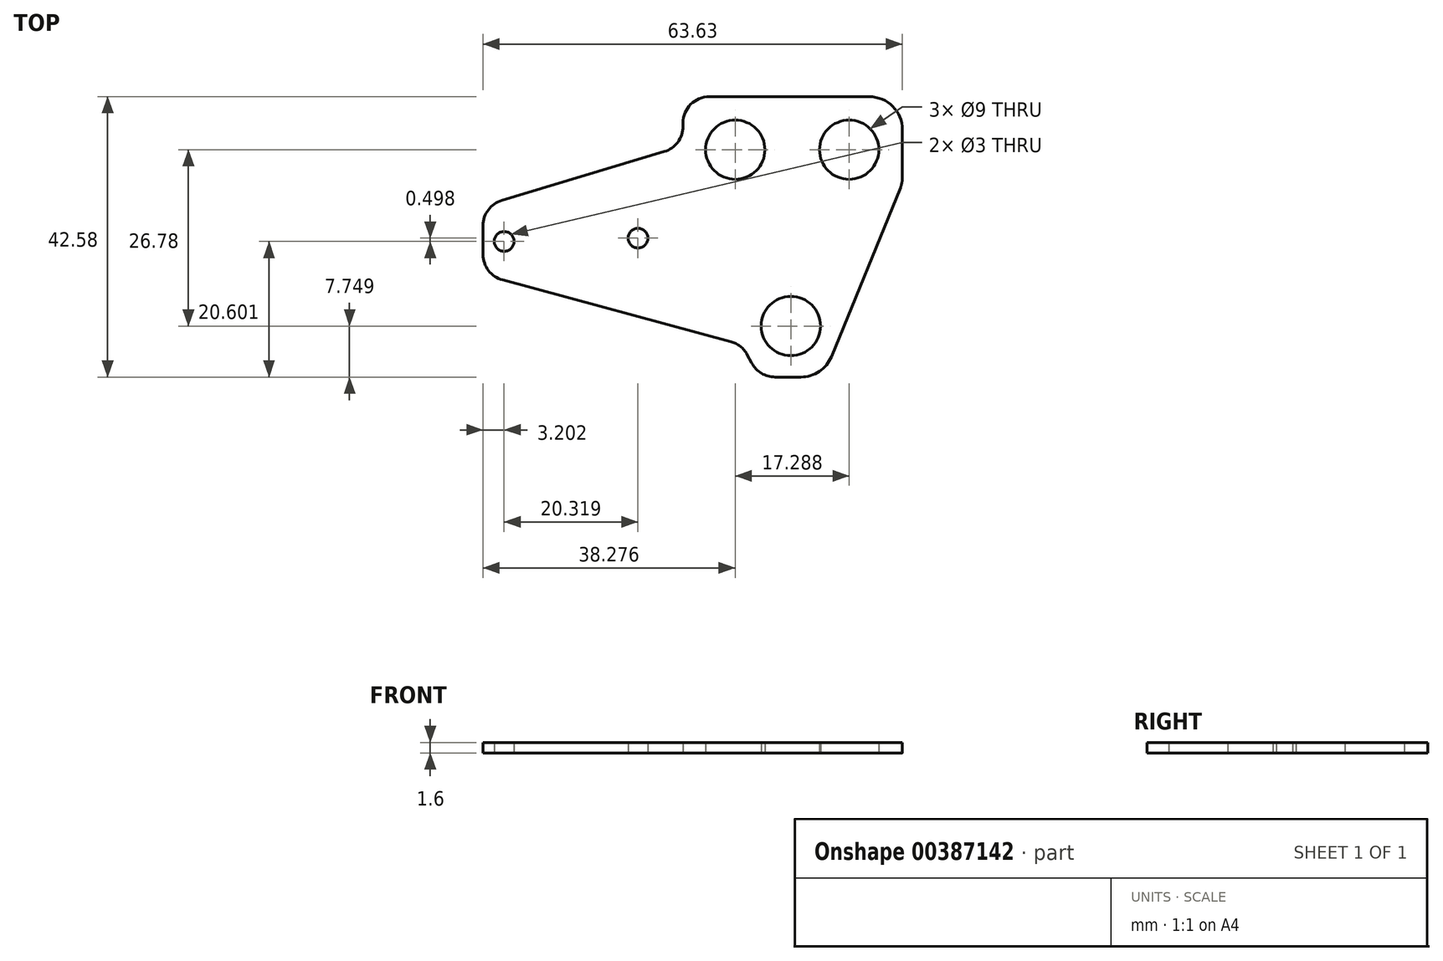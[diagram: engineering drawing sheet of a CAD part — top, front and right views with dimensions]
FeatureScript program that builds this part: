
annotation { "Feature Type Name" : "Feature", "Feature Type Description" : "" }
export const myFeature = defineFeature(function(context is Context, id is Id, definition is map)
    precondition{}
    {
        {
            var Q0;
            Q0=qCreatedBy(makeId("Top.planeOp"),FACE);
            var sketch = newSketch(context, id + "F0", { "sketchPlane" : qUnion([Q0])});
            skLineSegment(sketch, "E0", {"start": v(31.23, -1.42) * mm, "end": v(31.23, -8.72) * mm});
            skLineSegment(sketch, "E1", {"start": v(30.94, -10.23) * mm, "end": v(20.46, -35.89) * mm});
            skLineSegment(sketch, "E2", {"start": v(15.83, -39) * mm, "end": v(11.9, -39) * mm});
            skLineSegment(sketch, "E3", {"start": v(8.39, -36.9) * mm, "end": v(7.68, -35.58) * mm});
            skLineSegment(sketch, "E4", {"start": v(5.2, -33.62) * mm, "end": v(-29.44, -24.24) * mm});
            skLineSegment(sketch, "E5", {"start": v(-32.4, -20.38) * mm, "end": v(-32.4, -15.99) * mm});
            skLineSegment(sketch, "E6", {"start": v(-29.55, -12.16) * mm, "end": v(-4.9, -4.77) * mm});
            skLineSegment(sketch, "E7", {"start": v(-2.05, -0.93) * mm, "end": v(-2.05, -0.42) * mm});
            skLineSegment(sketch, "E8", {"start": v(1.95, 3.58) * mm, "end": v(26.23, 3.58) * mm});
            skCircle(sketch, "E9", {"center": v(23.16, -4.47) * mm, "radius": 4.5 * mm});
            skCircle(sketch, "E10", {"center": v(5.88, -4.47) * mm, "radius": 4.5 * mm});
            skCircle(sketch, "E11", {"center": v(14.32, -31.25) * mm, "radius": 4.5 * mm});
            skCircle(sketch, "E12", {"center": v(-29.2, -18.4) * mm, "radius": 1.5 * mm});
            skCircle(sketch, "E13", {"center": v(-8.88, -17.9) * mm, "radius": 1.5 * mm});
            skArc(sketch, "E14.filletArc", {"start": v(31.23, -1.42) * mm, "mid": v(29.77, 2.12) * mm, "end": v(26.23, 3.58) * mm});
            skArc(sketch, "E15.filletArc", {"start": v(15.83, -39) * mm, "mid": v(18.62, -38.15) * mm, "end": v(20.46, -35.89) * mm});
            skArc(sketch, "E16.filletArc", {"start": v(-29.55, -12.16) * mm, "mid": v(-31.6, -13.6) * mm, "end": v(-32.4, -15.99) * mm});
            skArc(sketch, "E17.filletArc", {"start": v(-32.4, -20.38) * mm, "mid": v(-31.57, -22.81) * mm, "end": v(-29.44, -24.24) * mm});
            skArc(sketch, "E18.filletArc", {"start": v(-4.9, -4.77) * mm, "mid": v(-2.84, -3.32) * mm, "end": v(-2.05, -0.93) * mm});
            skArc(sketch, "E19.filletArc", {"start": v(1.95, 3.58) * mm, "mid": v(-0.88, 2.41) * mm, "end": v(-2.05, -0.42) * mm});
            skArc(sketch, "E20.filletArc", {"start": v(8.39, -36.9) * mm, "mid": v(9.86, -38.43) * mm, "end": v(11.9, -39) * mm});
            skArc(sketch, "E21.filletArc", {"start": v(7.68, -35.58) * mm, "mid": v(6.64, -34.34) * mm, "end": v(5.2, -33.62) * mm});
            skArc(sketch, "E22.filletArc", {"start": v(30.94, -10.23) * mm, "mid": v(31.16, -9.5) * mm, "end": v(31.23, -8.72) * mm});
            skSolve(sketch);
        }
        {
            var Q0;
            Q0=makeQuery(id+"F0.imprint","IMPRINT",FACE,{"disambiguationData":[TD([[makeQuery(id+"F0.imprint","IMPRINT",EDGE,{"derivedFrom":sQuery(id+"F0.wireOp",EDGE,"E0")}),-1.0]])]});
            extrude(context, id + "F1", {"entities" : qUnion([Q0]), "depth" : 1.6 * mm});
        }
    });
